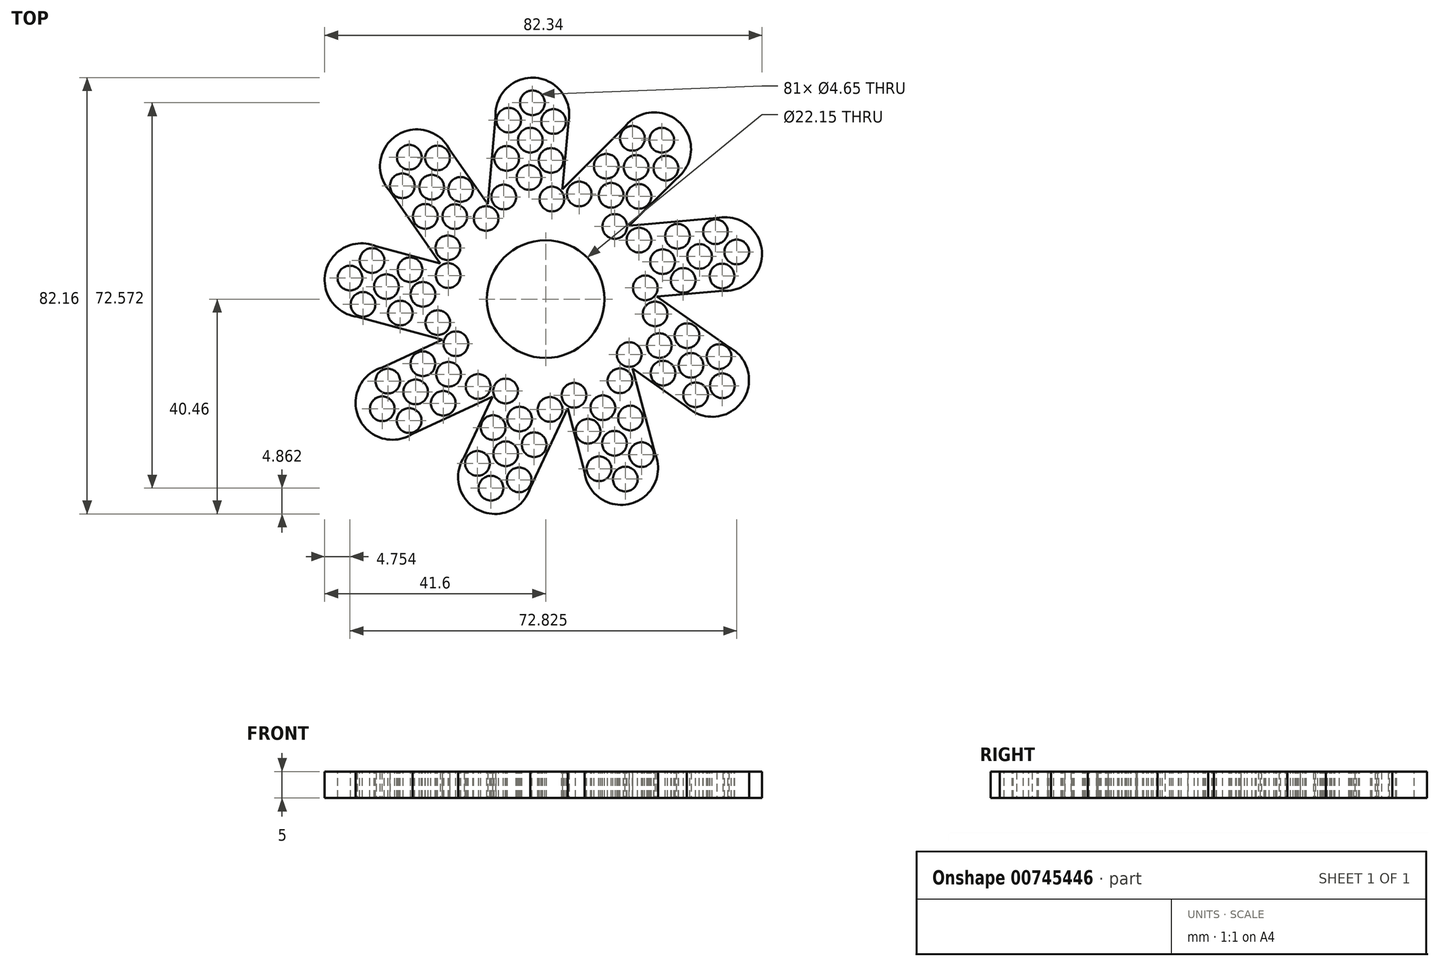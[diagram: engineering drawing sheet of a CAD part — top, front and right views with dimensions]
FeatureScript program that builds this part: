
annotation { "Feature Type Name" : "Feature", "Feature Type Description" : "" }
export const myFeature = defineFeature(function(context is Context, id is Id, definition is map)
    precondition{}
    {
        {
            var Q0;
            Q0=qCreatedBy(makeId("Top.planeOp"),FACE);
            var sketch = newSketch(context, id + "F0", { "sketchPlane" : qUnion([Q0])});
            skCircle(sketch, "E0", {"center": v(0, 0) * mm, "radius": 12.5 * mm});
            skLineSegment(sketch, "E1", {"start": v(-12.5, 0) * mm, "end": v(-9.34, 35.37) * mm});
            skLineSegment(sketch, "E2", {"start": v(-9.34, 35.37) * mm, "end": v(4.34, 34.15) * mm});
            skLineSegment(sketch, "E3", {"start": v(4.34, 34.15) * mm, "end": v(1.29, 0) * mm});
            skCircle(sketch, "E4", {"center": v(-2.5, 34.76) * mm, "radius": 6.94 * mm});
            skCircle(sketch, "E5.1.0", {"center": v(-24.26, 25.02) * mm, "radius": 6.94 * mm});
            skLineSegment(sketch, "E5.1.1", {"start": v(-18.63, 28.95) * mm, "end": v(0.99, 0.83) * mm});
            skLineSegment(sketch, "E5.1.2", {"start": v(-29.89, 21.1) * mm, "end": v(-18.63, 28.95) * mm});
            skLineSegment(sketch, "E5.1.3", {"start": v(-9.58, -8.03) * mm, "end": v(-29.89, 21.1) * mm});
            skCircle(sketch, "E5.2.0", {"center": v(-34.67, 3.58) * mm, "radius": 6.94 * mm});
            skLineSegment(sketch, "E5.2.1", {"start": v(-32.88, 10.2) * mm, "end": v(0.22, 1.27) * mm});
            skLineSegment(sketch, "E5.2.2", {"start": v(-36.46, -3.05) * mm, "end": v(-32.88, 10.2) * mm});
            skLineSegment(sketch, "E5.2.3", {"start": v(-2.17, -12.31) * mm, "end": v(-36.46, -3.05) * mm});
            skCircle(sketch, "E5.3.0", {"center": v(-28.86, -19.54) * mm, "radius": 6.94 * mm});
            skLineSegment(sketch, "E5.3.1", {"start": v(-31.75, -13.32) * mm, "end": v(-0.64, 1.11) * mm});
            skLineSegment(sketch, "E5.3.2", {"start": v(-25.97, -25.77) * mm, "end": v(-31.75, -13.32) * mm});
            skLineSegment(sketch, "E5.3.3", {"start": v(6.25, -10.83) * mm, "end": v(-25.97, -25.77) * mm});
            skCircle(sketch, "E5.4.0", {"center": v(-9.54, -33.52) * mm, "radius": 6.94 * mm});
            skLineSegment(sketch, "E5.4.1", {"start": v(-15.76, -30.6) * mm, "end": v(-1.2, 0.44) * mm});
            skLineSegment(sketch, "E5.4.2", {"start": v(-3.33, -36.43) * mm, "end": v(-15.76, -30.6) * mm});
            skLineSegment(sketch, "E5.4.3", {"start": v(11.75, -4.28) * mm, "end": v(-3.33, -36.43) * mm});
            skCircle(sketch, "E5.5.0", {"center": v(14.24, -31.81) * mm, "radius": 6.94 * mm});
            skLineSegment(sketch, "E5.5.1", {"start": v(7.6, -33.58) * mm, "end": v(-1.2, -0.44) * mm});
            skLineSegment(sketch, "E5.5.2", {"start": v(20.87, -30.05) * mm, "end": v(7.6, -33.58) * mm});
            skLineSegment(sketch, "E5.5.3", {"start": v(11.75, 4.28) * mm, "end": v(20.87, -30.05) * mm});
            skCircle(sketch, "E5.6.0", {"center": v(31.35, -15.22) * mm, "radius": 6.94 * mm});
            skLineSegment(sketch, "E5.6.1", {"start": v(27.4, -20.83) * mm, "end": v(-0.64, -1.11) * mm});
            skLineSegment(sketch, "E5.6.2", {"start": v(35.3, -9.6) * mm, "end": v(27.4, -20.83) * mm});
            skLineSegment(sketch, "E5.6.3", {"start": v(6.25, 10.83) * mm, "end": v(35.3, -9.6) * mm});
            skCircle(sketch, "E5.7.0", {"center": v(33.8, 8.5) * mm, "radius": 6.94 * mm});
            skLineSegment(sketch, "E5.7.1", {"start": v(34.39, 1.66) * mm, "end": v(0.22, -1.27) * mm});
            skLineSegment(sketch, "E5.7.2", {"start": v(33.22, 15.34) * mm, "end": v(34.39, 1.66) * mm});
            skLineSegment(sketch, "E5.7.3", {"start": v(-2.17, 12.31) * mm, "end": v(33.22, 15.34) * mm});
            skCircle(sketch, "E5.8.0", {"center": v(20.43, 28.23) * mm, "radius": 6.94 * mm});
            skLineSegment(sketch, "E5.8.1", {"start": v(25.28, 23.37) * mm, "end": v(0.99, -0.83) * mm});
            skLineSegment(sketch, "E5.8.2", {"start": v(15.59, 33.1) * mm, "end": v(25.28, 23.37) * mm});
            skLineSegment(sketch, "E5.8.3", {"start": v(-9.58, 8.03) * mm, "end": v(15.59, 33.1) * mm});
            skSolve(sketch);
        }
        {
            var Q0;
            {var subQ0=sQuery(id+"F0.wireOp",EDGE,"E5.5.1");var subQ1=sQuery(id+"F0.wireOp",EDGE,"E5.4.3");var subQ2=makeQuery(id+"F0.imprint","INTERSECT",VERTEX,{"derivedFrom":[subQ1,subQ0]});Q0=makeQuery(id+"F0.imprint","IMPRINT",FACE,{"disambiguationData":[TD([[makeQuery(id+"F0.imprint","IMPRINT",EDGE,{"disambiguationData":[TD([[subQ2,1.0]])],"derivedFrom":subQ1}),1.0]])]});}
            var Q1;
            {var subQ5=sQuery(id+"F0.wireOp",EDGE,"E5.8.2");Q1=makeQuery(id+"F0.imprint","IMPRINT",FACE,{"disambiguationData":[TD([[makeQuery(id+"F0.imprint","IMPRINT",EDGE,{"derivedFrom":subQ5}),-1.0]])]});}
            var Q2;
            {var subQ5=sQuery(id+"F0.wireOp",EDGE,"E5.2.2");Q2=makeQuery(id+"F0.imprint","IMPRINT",FACE,{"disambiguationData":[TD([[makeQuery(id+"F0.imprint","IMPRINT",EDGE,{"derivedFrom":subQ5}),-1.0]])]});}
            var Q3;
            {var subQ5=sQuery(id+"F0.wireOp",EDGE,"E5.2.3");var subQ6=sQuery(id+"F0.wireOp",EDGE,"E0");var subQ10=makeQuery(id+"F0.imprint","INTERSECT",VERTEX,{"disambiguationData":[OD(0.0)],"derivedFrom":[subQ6,subQ5]});Q3=makeQuery(id+"F0.imprint","IMPRINT",FACE,{"disambiguationData":[TD([[makeQuery(id+"F0.imprint","IMPRINT",EDGE,{"disambiguationData":[TD([[subQ10,1.0]])],"derivedFrom":subQ6}),-1.0]])]});}
            var Q4;
            {var subQ5=sQuery(id+"F0.wireOp",EDGE,"E5.1.2");Q4=makeQuery(id+"F0.imprint","IMPRINT",FACE,{"disambiguationData":[TD([[makeQuery(id+"F0.imprint","IMPRINT",EDGE,{"derivedFrom":subQ5}),-1.0]])]});}
            var Q5;
            {var subQ5=sQuery(id+"F0.wireOp",EDGE,"E5.5.3");var subQ6=sQuery(id+"F0.wireOp",EDGE,"E0");var subQ7=makeQuery(id+"F0.imprint","INTERSECT",VERTEX,{"disambiguationData":[OD(0.0)],"derivedFrom":[subQ6,subQ5]});Q5=makeQuery(id+"F0.imprint","IMPRINT",FACE,{"disambiguationData":[TD([[makeQuery(id+"F0.imprint","IMPRINT",EDGE,{"disambiguationData":[TD([[subQ7,1.0]])],"derivedFrom":subQ6}),-1.0]])]});}
            var Q6;
            {var subQ5=sQuery(id+"F0.wireOp",EDGE,"E5.3.3");var subQ6=sQuery(id+"F0.wireOp",EDGE,"E0");var subQ7=makeQuery(id+"F0.imprint","INTERSECT",VERTEX,{"disambiguationData":[OD(0.0)],"derivedFrom":[subQ6,subQ5]});Q6=makeQuery(id+"F0.imprint","IMPRINT",FACE,{"disambiguationData":[TD([[makeQuery(id+"F0.imprint","IMPRINT",EDGE,{"disambiguationData":[TD([[subQ7,1.0]])],"derivedFrom":subQ6}),-1.0]])]});}
            var Q7;
            {var subQ0=sQuery(id+"F0.wireOp",EDGE,"E5.1.1");var subQ1=sQuery(id+"F0.wireOp",EDGE,"E1");var subQ2=makeQuery(id+"F0.imprint","INTERSECT",VERTEX,{"derivedFrom":[subQ1,subQ0]});Q7=makeQuery(id+"F0.imprint","IMPRINT",FACE,{"disambiguationData":[TD([[makeQuery(id+"F0.imprint","IMPRINT",EDGE,{"disambiguationData":[TD([[subQ2,1.0]])],"derivedFrom":subQ1}),1.0]])]});}
            var Q8;
            {var subQ0=sQuery(id+"F0.wireOp",EDGE,"E5.6.1");var subQ1=sQuery(id+"F0.wireOp",EDGE,"E5.5.3");var subQ2=makeQuery(id+"F0.imprint","INTERSECT",VERTEX,{"derivedFrom":[subQ1,subQ0]});Q8=makeQuery(id+"F0.imprint","IMPRINT",FACE,{"disambiguationData":[TD([[makeQuery(id+"F0.imprint","IMPRINT",EDGE,{"disambiguationData":[TD([[subQ2,1.0]])],"derivedFrom":subQ1}),1.0]])]});}
            var Q9;
            {var subQ5=sQuery(id+"F0.wireOp",EDGE,"E5.3.2");Q9=makeQuery(id+"F0.imprint","IMPRINT",FACE,{"disambiguationData":[TD([[makeQuery(id+"F0.imprint","IMPRINT",EDGE,{"derivedFrom":subQ5}),-1.0]])]});}
            var Q10;
            {var subQ0=sQuery(id+"F0.wireOp",EDGE,"E5.6.3");var subQ1=sQuery(id+"F0.wireOp",EDGE,"E0");var subQ9=makeQuery(id+"F0.imprint","INTERSECT",VERTEX,{"disambiguationData":[OD(0.0)],"derivedFrom":[subQ1,subQ0]});Q10=makeQuery(id+"F0.imprint","IMPRINT",FACE,{"disambiguationData":[TD([[makeQuery(id+"F0.imprint","IMPRINT",EDGE,{"disambiguationData":[TD([[subQ9,1.0]])],"derivedFrom":subQ1}),-1.0]])]});}
            var Q11;
            {var subQ5=sQuery(id+"F0.wireOp",EDGE,"E5.4.3");var subQ6=sQuery(id+"F0.wireOp",EDGE,"E0");var subQ10=makeQuery(id+"F0.imprint","INTERSECT",VERTEX,{"disambiguationData":[OD(0.0)],"derivedFrom":[subQ6,subQ5]});Q11=makeQuery(id+"F0.imprint","IMPRINT",FACE,{"disambiguationData":[TD([[makeQuery(id+"F0.imprint","IMPRINT",EDGE,{"disambiguationData":[TD([[subQ10,1.0]])],"derivedFrom":subQ6}),-1.0]])]});}
            var Q12;
            {var subQ0=sQuery(id+"F0.wireOp",EDGE,"E5.1.1");var subQ1=sQuery(id+"F0.wireOp",EDGE,"E1");var subQ2=makeQuery(id+"F0.imprint","INTERSECT",VERTEX,{"derivedFrom":[subQ1,subQ0]});Q12=makeQuery(id+"F0.imprint","IMPRINT",FACE,{"disambiguationData":[TD([[makeQuery(id+"F0.imprint","IMPRINT",EDGE,{"disambiguationData":[TD([[subQ2,-1.0]])],"derivedFrom":subQ1}),-1.0]])]});}
            var Q13;
            {var subQ0=sQuery(id+"F0.wireOp",EDGE,"E5.7.1");var subQ1=sQuery(id+"F0.wireOp",EDGE,"E5.6.3");var subQ2=makeQuery(id+"F0.imprint","INTERSECT",VERTEX,{"derivedFrom":[subQ1,subQ0]});Q13=makeQuery(id+"F0.imprint","IMPRINT",FACE,{"disambiguationData":[TD([[makeQuery(id+"F0.imprint","IMPRINT",EDGE,{"disambiguationData":[TD([[subQ2,1.0]])],"derivedFrom":subQ1}),1.0]])]});}
            var Q14;
            {var subQ1=sQuery(id+"F0.wireOp",EDGE,"E0");var subQ8=sQuery(id+"F0.wireOp",EDGE,"E5.5.3");var subQ31=makeQuery(id+"F0.imprint","INTERSECT",VERTEX,{"disambiguationData":[OD(0.0)],"derivedFrom":[subQ1,subQ8]});Q14=makeQuery(id+"F0.imprint","IMPRINT",FACE,{"disambiguationData":[TD([[makeQuery(id+"F0.imprint","IMPRINT",EDGE,{"disambiguationData":[TD([[subQ31,-1.0]])],"derivedFrom":subQ1}),1.0]])]});}
            var Q15;
            {var subQ5=sQuery(id+"F0.wireOp",EDGE,"E5.8.3");var subQ7=sQuery(id+"F0.wireOp",EDGE,"E3");var subQ8=makeQuery(id+"F0.imprint","INTERSECT",VERTEX,{"derivedFrom":[subQ7,subQ5]});Q15=makeQuery(id+"F0.imprint","IMPRINT",FACE,{"disambiguationData":[TD([[makeQuery(id+"F0.imprint","IMPRINT",EDGE,{"disambiguationData":[TD([[subQ8,-1.0]])],"derivedFrom":subQ7}),1.0]])]});}
            var Q16;
            {var subQ5=sQuery(id+"F0.wireOp",EDGE,"E5.4.2");Q16=makeQuery(id+"F0.imprint","IMPRINT",FACE,{"disambiguationData":[TD([[makeQuery(id+"F0.imprint","IMPRINT",EDGE,{"derivedFrom":subQ5}),-1.0]])]});}
            var Q17;
            {var subQ3=sQuery(id+"F0.wireOp",EDGE,"E5.8.3");var subQ5=sQuery(id+"F0.wireOp",EDGE,"E0");var subQ6=makeQuery(id+"F0.imprint","INTERSECT",VERTEX,{"disambiguationData":[OD(0.0)],"derivedFrom":[subQ5,subQ3]});Q17=makeQuery(id+"F0.imprint","IMPRINT",FACE,{"disambiguationData":[TD([[makeQuery(id+"F0.imprint","IMPRINT",EDGE,{"disambiguationData":[TD([[subQ6,1.0]])],"derivedFrom":subQ5}),-1.0]])]});}
            var Q18;
            {var subQ0=sQuery(id+"F0.wireOp",EDGE,"E2");Q18=makeQuery(id+"F0.imprint","IMPRINT",FACE,{"disambiguationData":[TD([[makeQuery(id+"F0.imprint","IMPRINT",EDGE,{"derivedFrom":subQ0}),1.0]])]});}
            var Q19;
            {var subQ5=sQuery(id+"F0.wireOp",EDGE,"E5.1.2");Q19=makeQuery(id+"F0.imprint","IMPRINT",FACE,{"disambiguationData":[TD([[makeQuery(id+"F0.imprint","IMPRINT",EDGE,{"derivedFrom":subQ5}),1.0]])]});}
            var Q20;
            {var subQ5=sQuery(id+"F0.wireOp",EDGE,"E5.2.2");Q20=makeQuery(id+"F0.imprint","IMPRINT",FACE,{"disambiguationData":[TD([[makeQuery(id+"F0.imprint","IMPRINT",EDGE,{"derivedFrom":subQ5}),1.0]])]});}
            var Q21;
            {var subQ5=sQuery(id+"F0.wireOp",EDGE,"E5.3.2");Q21=makeQuery(id+"F0.imprint","IMPRINT",FACE,{"disambiguationData":[TD([[makeQuery(id+"F0.imprint","IMPRINT",EDGE,{"derivedFrom":subQ5}),1.0]])]});}
            var Q22;
            {var subQ5=sQuery(id+"F0.wireOp",EDGE,"E5.4.2");Q22=makeQuery(id+"F0.imprint","IMPRINT",FACE,{"disambiguationData":[TD([[makeQuery(id+"F0.imprint","IMPRINT",EDGE,{"derivedFrom":subQ5}),1.0]])]});}
            var Q23;
            {var subQ5=sQuery(id+"F0.wireOp",EDGE,"E5.5.2");Q23=makeQuery(id+"F0.imprint","IMPRINT",FACE,{"disambiguationData":[TD([[makeQuery(id+"F0.imprint","IMPRINT",EDGE,{"derivedFrom":subQ5}),1.0]])]});}
            var Q24;
            {var subQ5=sQuery(id+"F0.wireOp",EDGE,"E5.6.2");Q24=makeQuery(id+"F0.imprint","IMPRINT",FACE,{"disambiguationData":[TD([[makeQuery(id+"F0.imprint","IMPRINT",EDGE,{"derivedFrom":subQ5}),1.0]])]});}
            var Q25;
            {var subQ5=sQuery(id+"F0.wireOp",EDGE,"E5.7.2");Q25=makeQuery(id+"F0.imprint","IMPRINT",FACE,{"disambiguationData":[TD([[makeQuery(id+"F0.imprint","IMPRINT",EDGE,{"derivedFrom":subQ5}),1.0]])]});}
            var Q26;
            {var subQ5=sQuery(id+"F0.wireOp",EDGE,"E5.8.2");Q26=makeQuery(id+"F0.imprint","IMPRINT",FACE,{"disambiguationData":[TD([[makeQuery(id+"F0.imprint","IMPRINT",EDGE,{"derivedFrom":subQ5}),1.0]])]});}
            var Q27;
            {var subQ0=sQuery(id+"F0.wireOp",EDGE,"E5.2.1");var subQ1=sQuery(id+"F0.wireOp",EDGE,"E5.1.3");var subQ2=makeQuery(id+"F0.imprint","INTERSECT",VERTEX,{"derivedFrom":[subQ1,subQ0]});Q27=makeQuery(id+"F0.imprint","IMPRINT",FACE,{"disambiguationData":[TD([[makeQuery(id+"F0.imprint","IMPRINT",EDGE,{"disambiguationData":[TD([[subQ2,1.0]])],"derivedFrom":subQ1}),1.0]])]});}
            var Q28;
            {var subQ5=sQuery(id+"F0.wireOp",EDGE,"E5.5.2");Q28=makeQuery(id+"F0.imprint","IMPRINT",FACE,{"disambiguationData":[TD([[makeQuery(id+"F0.imprint","IMPRINT",EDGE,{"derivedFrom":subQ5}),-1.0]])]});}
            var Q29;
            {var subQ5=sQuery(id+"F0.wireOp",EDGE,"E1");var subQ6=sQuery(id+"F0.wireOp",EDGE,"E0");var subQ9=makeQuery(id+"F0.imprint","INTERSECT",VERTEX,{"disambiguationData":[OD(0.0)],"derivedFrom":[subQ6,subQ5]});Q29=makeQuery(id+"F0.imprint","IMPRINT",FACE,{"disambiguationData":[TD([[makeQuery(id+"F0.imprint","IMPRINT",EDGE,{"disambiguationData":[TD([[subQ9,1.0]])],"derivedFrom":subQ6}),-1.0]])]});}
            var Q30;
            {var subQ0=sQuery(id+"F0.wireOp",EDGE,"E5.3.1");var subQ1=sQuery(id+"F0.wireOp",EDGE,"E5.2.3");var subQ2=makeQuery(id+"F0.imprint","INTERSECT",VERTEX,{"derivedFrom":[subQ1,subQ0]});Q30=makeQuery(id+"F0.imprint","IMPRINT",FACE,{"disambiguationData":[TD([[makeQuery(id+"F0.imprint","IMPRINT",EDGE,{"disambiguationData":[TD([[subQ2,1.0]])],"derivedFrom":subQ1}),1.0]])]});}
            var Q31;
            {var subQ5=sQuery(id+"F0.wireOp",EDGE,"E5.6.2");Q31=makeQuery(id+"F0.imprint","IMPRINT",FACE,{"disambiguationData":[TD([[makeQuery(id+"F0.imprint","IMPRINT",EDGE,{"derivedFrom":subQ5}),-1.0]])]});}
            var Q32;
            {var subQ0=sQuery(id+"F0.wireOp",EDGE,"E2");Q32=makeQuery(id+"F0.imprint","IMPRINT",FACE,{"disambiguationData":[TD([[makeQuery(id+"F0.imprint","IMPRINT",EDGE,{"derivedFrom":subQ0}),-1.0]])]});}
            var Q33;
            {var subQ0=sQuery(id+"F0.wireOp",EDGE,"E5.1.3");var subQ1=sQuery(id+"F0.wireOp",EDGE,"E0");var subQ9=makeQuery(id+"F0.imprint","INTERSECT",VERTEX,{"disambiguationData":[OD(0.0)],"derivedFrom":[subQ1,subQ0]});Q33=makeQuery(id+"F0.imprint","IMPRINT",FACE,{"disambiguationData":[TD([[makeQuery(id+"F0.imprint","IMPRINT",EDGE,{"disambiguationData":[TD([[subQ9,1.0]])],"derivedFrom":subQ1}),-1.0]])]});}
            var Q34;
            {var subQ0=sQuery(id+"F0.wireOp",EDGE,"E5.4.1");var subQ1=sQuery(id+"F0.wireOp",EDGE,"E5.3.3");var subQ2=makeQuery(id+"F0.imprint","INTERSECT",VERTEX,{"derivedFrom":[subQ1,subQ0]});Q34=makeQuery(id+"F0.imprint","IMPRINT",FACE,{"disambiguationData":[TD([[makeQuery(id+"F0.imprint","IMPRINT",EDGE,{"disambiguationData":[TD([[subQ2,1.0]])],"derivedFrom":subQ1}),1.0]])]});}
            var Q35;
            {var subQ5=sQuery(id+"F0.wireOp",EDGE,"E5.7.2");Q35=makeQuery(id+"F0.imprint","IMPRINT",FACE,{"disambiguationData":[TD([[makeQuery(id+"F0.imprint","IMPRINT",EDGE,{"derivedFrom":subQ5}),-1.0]])]});}
            var Q36;
            {var subQ1=sQuery(id+"F0.wireOp",EDGE,"E0");var subQ7=sQuery(id+"F0.wireOp",EDGE,"E5.7.3");var subQ9=makeQuery(id+"F0.imprint","INTERSECT",VERTEX,{"disambiguationData":[OD(0.0)],"derivedFrom":[subQ1,subQ7]});Q36=makeQuery(id+"F0.imprint","IMPRINT",FACE,{"disambiguationData":[TD([[makeQuery(id+"F0.imprint","IMPRINT",EDGE,{"disambiguationData":[TD([[subQ9,1.0]])],"derivedFrom":subQ1}),-1.0]])]});}
            var Q37;
            {var subQ0=sQuery(id+"F0.wireOp",EDGE,"E5.7.1");var subQ1=sQuery(id+"F0.wireOp",EDGE,"E0");var subQ2=makeQuery(id+"F0.imprint","INTERSECT",VERTEX,{"derivedFrom":[subQ1,subQ0]});Q37=makeQuery(id+"F0.imprint","IMPRINT",FACE,{"disambiguationData":[TD([[makeQuery(id+"F0.imprint","IMPRINT",EDGE,{"disambiguationData":[TD([[subQ2,-1.0]])],"derivedFrom":subQ1}),-1.0]])]});}
            var Q38;
            {var subQ0=sQuery(id+"F0.wireOp",EDGE,"E5.1.1");var subQ1=sQuery(id+"F0.wireOp",EDGE,"E0");var subQ2=makeQuery(id+"F0.imprint","INTERSECT",VERTEX,{"derivedFrom":[subQ1,subQ0]});Q38=makeQuery(id+"F0.imprint","IMPRINT",FACE,{"disambiguationData":[TD([[makeQuery(id+"F0.imprint","IMPRINT",EDGE,{"disambiguationData":[TD([[subQ2,-1.0]])],"derivedFrom":subQ1}),-1.0]])]});}
            var Q39;
            {var subQ0=sQuery(id+"F0.wireOp",EDGE,"E5.8.1");var subQ1=sQuery(id+"F0.wireOp",EDGE,"E0");var subQ2=makeQuery(id+"F0.imprint","INTERSECT",VERTEX,{"derivedFrom":[subQ1,subQ0]});Q39=makeQuery(id+"F0.imprint","IMPRINT",FACE,{"disambiguationData":[TD([[makeQuery(id+"F0.imprint","IMPRINT",EDGE,{"disambiguationData":[TD([[subQ2,-1.0]])],"derivedFrom":subQ1}),-1.0]])]});}
            var Q40;
            {var subQ0=sQuery(id+"F0.wireOp",EDGE,"E5.2.1");var subQ1=sQuery(id+"F0.wireOp",EDGE,"E0");var subQ2=makeQuery(id+"F0.imprint","INTERSECT",VERTEX,{"derivedFrom":[subQ1,subQ0]});Q40=makeQuery(id+"F0.imprint","IMPRINT",FACE,{"disambiguationData":[TD([[makeQuery(id+"F0.imprint","IMPRINT",EDGE,{"disambiguationData":[TD([[subQ2,-1.0]])],"derivedFrom":subQ1}),-1.0]])]});}
            var Q41;
            {var subQ0=sQuery(id+"F0.wireOp",EDGE,"E3");var subQ1=sQuery(id+"F0.wireOp",EDGE,"E0");var subQ2=makeQuery(id+"F0.imprint","INTERSECT",VERTEX,{"derivedFrom":[subQ1,subQ0]});Q41=makeQuery(id+"F0.imprint","IMPRINT",FACE,{"disambiguationData":[TD([[makeQuery(id+"F0.imprint","IMPRINT",EDGE,{"disambiguationData":[TD([[subQ2,-1.0]])],"derivedFrom":subQ1}),-1.0]])]});}
            var Q42;
            {var subQ0=sQuery(id+"F0.wireOp",EDGE,"E5.2.3");var subQ1=sQuery(id+"F0.wireOp",EDGE,"E0");var subQ2=makeQuery(id+"F0.imprint","INTERSECT",VERTEX,{"disambiguationData":[OD(0.0)],"derivedFrom":[subQ1,subQ0]});Q42=makeQuery(id+"F0.imprint","IMPRINT",FACE,{"disambiguationData":[TD([[makeQuery(id+"F0.imprint","IMPRINT",EDGE,{"disambiguationData":[TD([[subQ2,1.0]])],"derivedFrom":subQ1}),1.0]])]});}
            var Q43;
            {var subQ0=sQuery(id+"F0.wireOp",EDGE,"E1");var subQ1=sQuery(id+"F0.wireOp",EDGE,"E0");var subQ2=makeQuery(id+"F0.imprint","INTERSECT",VERTEX,{"disambiguationData":[OD(0.0)],"derivedFrom":[subQ1,subQ0]});Q43=makeQuery(id+"F0.imprint","IMPRINT",FACE,{"disambiguationData":[TD([[makeQuery(id+"F0.imprint","IMPRINT",EDGE,{"disambiguationData":[TD([[subQ2,1.0]])],"derivedFrom":subQ1}),1.0]])]});}
            var Q44;
            {var subQ0=sQuery(id+"F0.wireOp",EDGE,"E5.1.3");var subQ1=sQuery(id+"F0.wireOp",EDGE,"E0");var subQ2=makeQuery(id+"F0.imprint","INTERSECT",VERTEX,{"disambiguationData":[OD(0.0)],"derivedFrom":[subQ1,subQ0]});Q44=makeQuery(id+"F0.imprint","IMPRINT",FACE,{"disambiguationData":[TD([[makeQuery(id+"F0.imprint","IMPRINT",EDGE,{"disambiguationData":[TD([[subQ2,1.0]])],"derivedFrom":subQ1}),1.0]])]});}
            var Q45;
            {var subQ0=sQuery(id+"F0.wireOp",EDGE,"E5.3.3");var subQ1=sQuery(id+"F0.wireOp",EDGE,"E0");var subQ2=makeQuery(id+"F0.imprint","INTERSECT",VERTEX,{"disambiguationData":[OD(0.0)],"derivedFrom":[subQ1,subQ0]});Q45=makeQuery(id+"F0.imprint","IMPRINT",FACE,{"disambiguationData":[TD([[makeQuery(id+"F0.imprint","IMPRINT",EDGE,{"disambiguationData":[TD([[subQ2,1.0]])],"derivedFrom":subQ1}),1.0]])]});}
            var Q46;
            {var subQ0=sQuery(id+"F0.wireOp",EDGE,"E5.4.1");var subQ1=sQuery(id+"F0.wireOp",EDGE,"E0");var subQ2=makeQuery(id+"F0.imprint","INTERSECT",VERTEX,{"derivedFrom":[subQ1,subQ0]});Q46=makeQuery(id+"F0.imprint","IMPRINT",FACE,{"disambiguationData":[TD([[makeQuery(id+"F0.imprint","IMPRINT",EDGE,{"disambiguationData":[TD([[subQ2,-1.0]])],"derivedFrom":subQ1}),-1.0]])]});}
            var Q47;
            {var subQ0=sQuery(id+"F0.wireOp",EDGE,"E5.5.3");var subQ1=sQuery(id+"F0.wireOp",EDGE,"E0");var subQ2=makeQuery(id+"F0.imprint","INTERSECT",VERTEX,{"disambiguationData":[OD(0.0)],"derivedFrom":[subQ1,subQ0]});Q47=makeQuery(id+"F0.imprint","IMPRINT",FACE,{"disambiguationData":[TD([[makeQuery(id+"F0.imprint","IMPRINT",EDGE,{"disambiguationData":[TD([[subQ2,1.0]])],"derivedFrom":subQ1}),1.0]])]});}
            var Q48;
            {var subQ0=sQuery(id+"F0.wireOp",EDGE,"E5.6.3");var subQ1=sQuery(id+"F0.wireOp",EDGE,"E0");var subQ2=makeQuery(id+"F0.imprint","INTERSECT",VERTEX,{"disambiguationData":[OD(0.0)],"derivedFrom":[subQ1,subQ0]});Q48=makeQuery(id+"F0.imprint","IMPRINT",FACE,{"disambiguationData":[TD([[makeQuery(id+"F0.imprint","IMPRINT",EDGE,{"disambiguationData":[TD([[subQ2,1.0]])],"derivedFrom":subQ1}),1.0]])]});}
            var Q49;
            {var subQ0=sQuery(id+"F0.wireOp",EDGE,"E5.7.3");var subQ1=sQuery(id+"F0.wireOp",EDGE,"E0");var subQ2=makeQuery(id+"F0.imprint","INTERSECT",VERTEX,{"disambiguationData":[OD(0.0)],"derivedFrom":[subQ1,subQ0]});Q49=makeQuery(id+"F0.imprint","IMPRINT",FACE,{"disambiguationData":[TD([[makeQuery(id+"F0.imprint","IMPRINT",EDGE,{"disambiguationData":[TD([[subQ2,1.0]])],"derivedFrom":subQ1}),1.0]])]});}
            var Q50;
            {var subQ0=sQuery(id+"F0.wireOp",EDGE,"E5.8.3");var subQ1=sQuery(id+"F0.wireOp",EDGE,"E0");var subQ2=makeQuery(id+"F0.imprint","INTERSECT",VERTEX,{"disambiguationData":[OD(0.0)],"derivedFrom":[subQ1,subQ0]});Q50=makeQuery(id+"F0.imprint","IMPRINT",FACE,{"disambiguationData":[TD([[makeQuery(id+"F0.imprint","IMPRINT",EDGE,{"disambiguationData":[TD([[subQ2,1.0]])],"derivedFrom":subQ1}),1.0]])]});}
            var Q51;
            {var subQ0=sQuery(id+"F0.wireOp",EDGE,"E5.4.3");var subQ1=sQuery(id+"F0.wireOp",EDGE,"E0");var subQ2=makeQuery(id+"F0.imprint","INTERSECT",VERTEX,{"disambiguationData":[OD(0.0)],"derivedFrom":[subQ1,subQ0]});Q51=makeQuery(id+"F0.imprint","IMPRINT",FACE,{"disambiguationData":[TD([[makeQuery(id+"F0.imprint","IMPRINT",EDGE,{"disambiguationData":[TD([[subQ2,1.0]])],"derivedFrom":subQ1}),1.0]])]});}
            var Q52;
            {var subQ0=sQuery(id+"F0.wireOp",EDGE,"E5.5.1");var subQ1=sQuery(id+"F0.wireOp",EDGE,"E0");var subQ2=makeQuery(id+"F0.imprint","INTERSECT",VERTEX,{"derivedFrom":[subQ1,subQ0]});Q52=makeQuery(id+"F0.imprint","IMPRINT",FACE,{"disambiguationData":[TD([[makeQuery(id+"F0.imprint","IMPRINT",EDGE,{"disambiguationData":[TD([[subQ2,-1.0]])],"derivedFrom":subQ1}),-1.0]])]});}
            var Q53;
            {var subQ0=sQuery(id+"F0.wireOp",EDGE,"E5.6.1");var subQ1=sQuery(id+"F0.wireOp",EDGE,"E0");var subQ2=makeQuery(id+"F0.imprint","INTERSECT",VERTEX,{"derivedFrom":[subQ1,subQ0]});Q53=makeQuery(id+"F0.imprint","IMPRINT",FACE,{"disambiguationData":[TD([[makeQuery(id+"F0.imprint","IMPRINT",EDGE,{"disambiguationData":[TD([[subQ2,-1.0]])],"derivedFrom":subQ1}),-1.0]])]});}
            var Q54;
            {var subQ0=sQuery(id+"F0.wireOp",EDGE,"E5.3.1");var subQ1=sQuery(id+"F0.wireOp",EDGE,"E0");var subQ2=makeQuery(id+"F0.imprint","INTERSECT",VERTEX,{"derivedFrom":[subQ1,subQ0]});Q54=makeQuery(id+"F0.imprint","IMPRINT",FACE,{"disambiguationData":[TD([[makeQuery(id+"F0.imprint","IMPRINT",EDGE,{"disambiguationData":[TD([[subQ2,-1.0]])],"derivedFrom":subQ1}),-1.0]])]});}
            extrude(context, id + "F1", {"entities" : qUnion([Q0, Q1, Q2, Q3, Q4, Q5, Q6, Q7, Q8, Q9, Q10, Q11, Q12, Q13, Q14, Q15, Q16, Q17, Q18, Q19, Q20, Q21, Q22, Q23, Q24, Q25, Q26, Q27, Q28, Q29, Q30, Q31, Q32, Q33, Q34, Q35, Q36, Q37, Q38, Q39, Q40, Q41, Q42, Q43, Q44, Q45, Q46, Q47, Q48, Q49, Q50, Q51, Q52, Q53, Q54]), "depth" : 5 * mm, "offsetDistance" : 25 * mm});
        }
        {
            var Q0;
            Q0=makeQuery(id+"F1.opExtrude","CAP_FACE",FACE,{"disambiguationData":[OSD([sQuery(id+"F0.wireOp",EDGE,"E1"),sQuery(id+"F0.wireOp",EDGE,"E3"),sQuery(id+"F0.wireOp",EDGE,"E4"),sQuery(id+"F0.wireOp",EDGE,"E5.1.0"),sQuery(id+"F0.wireOp",EDGE,"E5.1.1"),sQuery(id+"F0.wireOp",EDGE,"E5.1.3"),sQuery(id+"F0.wireOp",EDGE,"E5.2.0"),sQuery(id+"F0.wireOp",EDGE,"E5.2.1"),sQuery(id+"F0.wireOp",EDGE,"E5.2.3"),sQuery(id+"F0.wireOp",EDGE,"E5.3.0"),sQuery(id+"F0.wireOp",EDGE,"E5.3.1"),sQuery(id+"F0.wireOp",EDGE,"E5.3.3"),sQuery(id+"F0.wireOp",EDGE,"E5.4.0"),sQuery(id+"F0.wireOp",EDGE,"E5.4.1"),sQuery(id+"F0.wireOp",EDGE,"E5.4.3"),sQuery(id+"F0.wireOp",EDGE,"E5.5.0"),sQuery(id+"F0.wireOp",EDGE,"E5.5.1"),sQuery(id+"F0.wireOp",EDGE,"E5.5.3"),sQuery(id+"F0.wireOp",EDGE,"E5.6.0"),sQuery(id+"F0.wireOp",EDGE,"E5.6.1"),sQuery(id+"F0.wireOp",EDGE,"E5.6.3"),sQuery(id+"F0.wireOp",EDGE,"E5.7.0"),sQuery(id+"F0.wireOp",EDGE,"E5.7.1"),sQuery(id+"F0.wireOp",EDGE,"E5.7.3"),sQuery(id+"F0.wireOp",EDGE,"E5.8.0"),sQuery(id+"F0.wireOp",EDGE,"E5.8.1"),sQuery(id+"F0.wireOp",EDGE,"E5.8.3")])],"isStart":false});
            var sketch = newSketch(context, id + "F2", { "sketchPlane" : qUnion([Q0])});
            skCircle(sketch, "E6", {"center": v(-7.34, 26.5) * mm, "radius": 2.33 * mm});
            skCircle(sketch, "E7", {"center": v(-6.95, 33.7) * mm, "radius": 2.33 * mm});
            skCircle(sketch, "E8", {"center": v(1.49, 33.46) * mm, "radius": 2.33 * mm});
            skCircle(sketch, "E9", {"center": v(-2.5, 36.97) * mm, "radius": 2.33 * mm});
            skCircle(sketch, "E10", {"center": v(-2.89, 29.94) * mm, "radius": 2.33 * mm});
            skCircle(sketch, "E11", {"center": v(1.02, 26.11) * mm, "radius": 2.33 * mm});
            skCircle(sketch, "E12", {"center": v(-3.12, 22.9) * mm, "radius": 2.33 * mm});
            skCircle(sketch, "E13", {"center": v(-7.89, 19.23) * mm, "radius": 2.33 * mm});
            skCircle(sketch, "E14", {"center": v(1.18, 18.84) * mm, "radius": 2.33 * mm});
            skCircle(sketch, "E15", {"center": v(0, 0) * mm, "radius": 11.07 * mm});
            skCircle(sketch, "E16.1.0", {"center": v(-18.4, 9.66) * mm, "radius": 2.33 * mm});
            skCircle(sketch, "E16.1.1", {"center": v(-22.66, 15.58) * mm, "radius": 2.33 * mm});
            skCircle(sketch, "E16.1.2", {"center": v(-17.12, 15.54) * mm, "radius": 2.33 * mm});
            skCircle(sketch, "E16.1.3", {"center": v(-16, 20.66) * mm, "radius": 2.33 * mm});
            skCircle(sketch, "E16.1.4", {"center": v(-21.46, 21.08) * mm, "radius": 2.33 * mm});
            skCircle(sketch, "E16.1.5", {"center": v(-26.98, 21.34) * mm, "radius": 2.33 * mm});
            skCircle(sketch, "E16.1.6", {"center": v(-25.68, 26.72) * mm, "radius": 2.33 * mm});
            skCircle(sketch, "E16.1.7", {"center": v(-20.37, 26.59) * mm, "radius": 2.33 * mm});
            skCircle(sketch, "E16.1.8", {"center": v(-11.21, 15.2) * mm, "radius": 2.33 * mm});
            skCircle(sketch, "E16.2.0", {"center": v(-20.31, -4.43) * mm, "radius": 2.33 * mm});
            skCircle(sketch, "E16.2.1", {"center": v(-27.37, -2.63) * mm, "radius": 2.33 * mm});
            skCircle(sketch, "E16.2.2", {"center": v(-23.1, 0.9) * mm, "radius": 2.33 * mm});
            skCircle(sketch, "E16.2.3", {"center": v(-25.54, 5.54) * mm, "radius": 2.33 * mm});
            skCircle(sketch, "E16.2.4", {"center": v(-29.99, 2.35) * mm, "radius": 2.33 * mm});
            skCircle(sketch, "E16.2.5", {"center": v(-34.39, -1) * mm, "radius": 2.33 * mm});
            skCircle(sketch, "E16.2.6", {"center": v(-36.85, 3.96) * mm, "radius": 2.33 * mm});
            skCircle(sketch, "E16.2.7", {"center": v(-32.7, 7.28) * mm, "radius": 2.33 * mm});
            skCircle(sketch, "E16.2.8", {"center": v(-18.35, 4.43) * mm, "radius": 2.33 * mm});
            skCircle(sketch, "E16.3.0", {"center": v(-12.71, -16.45) * mm, "radius": 2.33 * mm});
            skCircle(sketch, "E16.3.1", {"center": v(-19.28, -19.6) * mm, "radius": 2.33 * mm});
            skCircle(sketch, "E16.3.2", {"center": v(-18.28, -14.16) * mm, "radius": 2.33 * mm});
            skCircle(sketch, "E16.3.3", {"center": v(-23.12, -12.17) * mm, "radius": 2.33 * mm});
            skCircle(sketch, "E16.3.4", {"center": v(-24.49, -17.47) * mm, "radius": 2.33 * mm});
            skCircle(sketch, "E16.3.5", {"center": v(-25.7, -22.87) * mm, "radius": 2.33 * mm});
            skCircle(sketch, "E16.3.6", {"center": v(-30.77, -20.65) * mm, "radius": 2.33 * mm});
            skCircle(sketch, "E16.3.7", {"center": v(-29.72, -15.44) * mm, "radius": 2.33 * mm});
            skCircle(sketch, "E16.3.8", {"center": v(-16.9, -8.4) * mm, "radius": 2.33 * mm});
            skCircle(sketch, "E16.4.0", {"center": v(0.84, -20.77) * mm, "radius": 2.33 * mm});
            skCircle(sketch, "E16.4.1", {"center": v(-2.16, -27.42) * mm, "radius": 2.33 * mm});
            skCircle(sketch, "E16.4.2", {"center": v(-4.9, -22.6) * mm, "radius": 2.33 * mm});
            skCircle(sketch, "E16.4.3", {"center": v(-9.89, -24.19) * mm, "radius": 2.33 * mm});
            skCircle(sketch, "E16.4.4", {"center": v(-7.53, -29.12) * mm, "radius": 2.33 * mm});
            skCircle(sketch, "E16.4.5", {"center": v(-5, -34.04) * mm, "radius": 2.33 * mm});
            skCircle(sketch, "E16.4.6", {"center": v(-10.3, -35.6) * mm, "radius": 2.33 * mm});
            skCircle(sketch, "E16.4.7", {"center": v(-12.84, -30.93) * mm, "radius": 2.33 * mm});
            skCircle(sketch, "E16.4.8", {"center": v(-7.55, -17.3) * mm, "radius": 2.33 * mm});
            skCircle(sketch, "E16.5.0", {"center": v(14, -15.38) * mm, "radius": 2.33 * mm});
            skCircle(sketch, "E16.5.1", {"center": v(15.96, -22.4) * mm, "radius": 2.33 * mm});
            skCircle(sketch, "E16.5.2", {"center": v(10.77, -20.46) * mm, "radius": 2.33 * mm});
            skCircle(sketch, "E16.5.3", {"center": v(7.97, -24.89) * mm, "radius": 2.33 * mm});
            skCircle(sketch, "E16.5.4", {"center": v(12.95, -27.15) * mm, "radius": 2.33 * mm});
            skCircle(sketch, "E16.5.5", {"center": v(18.06, -29.28) * mm, "radius": 2.33 * mm});
            skCircle(sketch, "E16.5.6", {"center": v(15, -33.9) * mm, "radius": 2.33 * mm});
            skCircle(sketch, "E16.5.7", {"center": v(10.04, -31.95) * mm, "radius": 2.33 * mm});
            skCircle(sketch, "E16.5.8", {"center": v(5.34, -18.1) * mm, "radius": 2.33 * mm});
            skCircle(sketch, "E16.6.0", {"center": v(20.6, -2.78) * mm, "radius": 2.33 * mm});
            skCircle(sketch, "E16.6.1", {"center": v(26.62, -6.9) * mm, "radius": 2.33 * mm});
            skCircle(sketch, "E16.6.2", {"center": v(21.4, -8.75) * mm, "radius": 2.33 * mm});
            skCircle(sketch, "E16.6.3", {"center": v(22.1, -13.94) * mm, "radius": 2.33 * mm});
            skCircle(sketch, "E16.6.4", {"center": v(27.37, -12.47) * mm, "radius": 2.33 * mm});
            skCircle(sketch, "E16.6.5", {"center": v(32.65, -10.83) * mm, "radius": 2.33 * mm});
            skCircle(sketch, "E16.6.6", {"center": v(33.27, -16.32) * mm, "radius": 2.33 * mm});
            skCircle(sketch, "E16.6.7", {"center": v(28.23, -18.02) * mm, "radius": 2.33 * mm});
            skCircle(sketch, "E16.6.8", {"center": v(15.73, -10.44) * mm, "radius": 2.33 * mm});
            skCircle(sketch, "E16.7.0", {"center": v(17.57, 11.1) * mm, "radius": 2.33 * mm});
            skCircle(sketch, "E16.7.1", {"center": v(24.82, 11.83) * mm, "radius": 2.33 * mm});
            skCircle(sketch, "E16.7.2", {"center": v(22.02, 7.05) * mm, "radius": 2.33 * mm});
            skCircle(sketch, "E16.7.3", {"center": v(25.9, 3.53) * mm, "radius": 2.33 * mm});
            skCircle(sketch, "E16.7.4", {"center": v(28.98, 8.04) * mm, "radius": 2.33 * mm});
            skCircle(sketch, "E16.7.5", {"center": v(31.97, 12.7) * mm, "radius": 2.33 * mm});
            skCircle(sketch, "E16.7.6", {"center": v(35.98, 8.88) * mm, "radius": 2.33 * mm});
            skCircle(sketch, "E16.7.7", {"center": v(33.2, 4.34) * mm, "radius": 2.33 * mm});
            skCircle(sketch, "E16.7.8", {"center": v(18.76, 2.11) * mm, "radius": 2.33 * mm});
            skCircle(sketch, "E16.8.0", {"center": v(6.32, 19.8) * mm, "radius": 2.33 * mm});
            skCircle(sketch, "E16.8.1", {"center": v(11.41, 25.02) * mm, "radius": 2.33 * mm});
            skCircle(sketch, "E16.8.2", {"center": v(12.33, 19.56) * mm, "radius": 2.33 * mm});
            skCircle(sketch, "E16.8.3", {"center": v(17.56, 19.35) * mm, "radius": 2.33 * mm});
            skCircle(sketch, "E16.8.4", {"center": v(17.03, 24.8) * mm, "radius": 2.33 * mm});
            skCircle(sketch, "E16.8.5", {"center": v(16.33, 30.28) * mm, "radius": 2.33 * mm});
            skCircle(sketch, "E16.8.6", {"center": v(21.85, 29.93) * mm, "radius": 2.33 * mm});
            skCircle(sketch, "E16.8.7", {"center": v(22.65, 24.67) * mm, "radius": 2.33 * mm});
            skCircle(sketch, "E16.8.8", {"center": v(13.01, 13.68) * mm, "radius": 2.33 * mm});
            skSolve(sketch);
        }
        {
            var Q0;
            Q0 = qSketchRegion(id + "F2", true);
            extrude(context, id + "F3", {"entities" : qUnion([Q0]), "operationType" : NewBodyOperationType.REMOVE, "oppositeDirection" : true, "depth" : 5 * mm, "offsetDistance" : 25 * mm});
        }
    });
